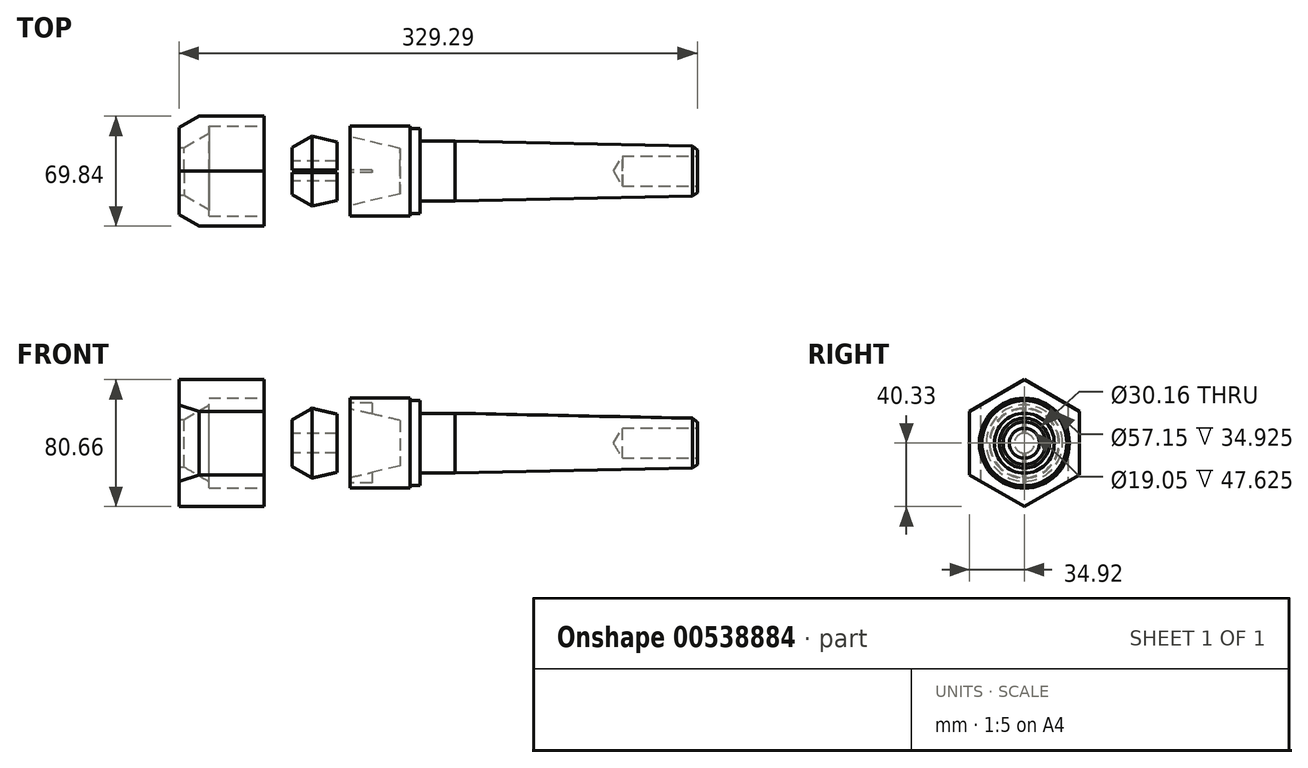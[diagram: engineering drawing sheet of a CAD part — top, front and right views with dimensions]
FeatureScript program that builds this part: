
annotation { "Feature Type Name" : "Feature", "Feature Type Description" : "" }
export const myFeature = defineFeature(function(context is Context, id is Id, definition is map)
    precondition{}
    {
        {
            var Q0;
            Q0=qCreatedBy(makeId("Front.planeOp"),FACE);
            var sketch = newSketch(context, id + "F0", { "sketchPlane" : qUnion([Q0])});
            skLineSegment(sketch, "E0.bottom", {"start": v(31.75, 0) * mm, "end": v(38.1, 0) * mm});
            skLineSegment(sketch, "E0.top", {"start": v(0, 28.58) * mm, "end": v(38.1, 28.58) * mm});
            skLineSegment(sketch, "E0.left", {"start": v(0, 21.83) * mm, "end": v(0, 28.58) * mm});
            skLineSegment(sketch, "E0.right", {"start": v(38.1, 0) * mm, "end": v(38.1, 28.58) * mm});
            skLineSegment(sketch, "E1.bottom", {"start": v(38.1, 0) * mm, "end": v(44.45, 0) * mm});
            skLineSegment(sketch, "E1.top", {"start": v(38.1, 26.99) * mm, "end": v(44.45, 26.99) * mm});
            skLineSegment(sketch, "E1.left", {"start": v(38.1, 0) * mm, "end": v(38.1, 26.99) * mm});
            skLineSegment(sketch, "E1.right", {"start": v(44.45, 0) * mm, "end": v(44.45, 26.99) * mm});
            skLineSegment(sketch, "E2.bottom", {"start": v(44.45, 0) * mm, "end": v(217.49, 0) * mm});
            skLineSegment(sketch, "E2.top", {"start": v(44.45, 19.02) * mm, "end": v(66.67, 19.02) * mm});
            skLineSegment(sketch, "E2.left", {"start": v(44.45, 0) * mm, "end": v(44.45, 19.02) * mm});
            skLineSegment(sketch, "E3.bottom", {"start": v(217.49, 0) * mm, "end": v(220.66, 0) * mm});
            skLineSegment(sketch, "E3.right", {"start": v(220.66, 0) * mm, "end": v(220.66, 13.5) * mm});
            skPoint(sketch, "E4", {"position": v(217.49, 15.88) * mm});
            skLineSegment(sketch, "E5", {"start": v(66.67, 19.02) * mm, "end": v(217.49, 15.87) * mm});
            skLineSegment(sketch, "E6", {"start": v(220.66, 13.5) * mm, "end": v(217.49, 15.88) * mm});
            skPoint(sketch, "E7.end.orphan", {"position": v(66.17, 0) * mm});
            skLineSegment(sketch, "E8", {"start": v(31.75, 0) * mm, "end": v(31.75, 14.5) * mm});
            skLineSegment(sketch, "E9", {"start": v(0, 21.83) * mm, "end": v(31.75, 14.5) * mm});
            skPoint(sketch, "E10", {"position": v(31.75, 14.5) * mm});
            skPoint(sketch, "E11.orphan", {"position": v(66.17, 6.55) * mm});
            skSolve(sketch);
        }
        {
            var Q0;
            Q0=makeQuery(id+"F0.imprint","IMPRINT",FACE,{"disambiguationData":[TD([[makeQuery(id+"F0.imprint","IMPRINT",EDGE,{"derivedFrom":sQuery(id+"F0.wireOp",EDGE,"E1.bottom")}),1.0]])]});
            var Q1;
            Q1=makeQuery(id+"F0.imprint","IMPRINT",FACE,{"disambiguationData":[TD([[makeQuery(id+"F0.imprint","IMPRINT",EDGE,{"derivedFrom":sQuery(id+"F0.wireOp",EDGE,"E0.bottom")}),1.0]])]});
            var Q2;
            Q2=makeQuery(id+"F0.imprint","IMPRINT",FACE,{"disambiguationData":[TD([[makeQuery(id+"F0.imprint","IMPRINT",EDGE,{"derivedFrom":sQuery(id+"F0.wireOp",EDGE,"E2.bottom")}),1.0]])]});
            var Q3;
            Q3=sQuery(id+"F0.wireOp",EDGE,"E2.bottom");
            revolve(context, id + "F1", {"entities" : qUnion([Q0, Q1, Q2]), "axis" : qUnion([Q3]), "revolveType" : RevolveType.FULL});
        }
        {
            var Q0;
            Q0=makeQuery(id+"F1.opRevolve","SWEPT_FACE",FACE,{"disambiguationData":[OSD([sQuery(id+"F0.wireOp",EDGE,"E3.right")])]});
            var sketch = newSketch(context, id + "F2", { "sketchPlane" : qUnion([Q0])});
            skCircle(sketch, "E12", {"center": v(0, 0) * mm, "radius": 9.53 * mm});
            skSolve(sketch);
        }
        {
            var Q0;
            Q0=sQuery(id+"F2.wireOp",VERTEX,"E12.center");
            var Q1;
            Q1=makeQuery(id+"F1.opRevolve","SWEPT_BODY",BODY,{"disambiguationData":[OSD([sQuery(id+"F0.wireOp",EDGE,"E0.bottom"),sQuery(id+"F0.wireOp",EDGE,"E0.top"),sQuery(id+"F0.wireOp",EDGE,"E0.left"),sQuery(id+"F0.wireOp",EDGE,"E0.right"),sQuery(id+"F0.wireOp",EDGE,"E1.bottom"),sQuery(id+"F0.wireOp",EDGE,"E1.top"),sQuery(id+"F0.wireOp",EDGE,"E1.right"),sQuery(id+"F0.wireOp",EDGE,"E2.bottom"),sQuery(id+"F0.wireOp",EDGE,"E2.top"),sQuery(id+"F0.wireOp",EDGE,"E3.bottom"),sQuery(id+"F0.wireOp",EDGE,"E3.right"),sQuery(id+"F0.wireOp",EDGE,"E5"),sQuery(id+"F0.wireOp",EDGE,"E6"),sQuery(id+"F0.wireOp",EDGE,"E8"),sQuery(id+"F0.wireOp",EDGE,"E9")])]});
            hole(context, id + "F3", {"style" : HoleStyle.SIMPLE, "endStyle" : HoleEndStyle.BLIND, "holeDiameter" : 19.05 * mm, "holeDepth" : 47.62 * mm, "isTappedThrough" : true, "tappedDepth" : 12.7 * mm, "tapClearance" : 3, "locations" : qUnion([Q0]), "scope" : qUnion([Q1])});
        }
        {
            var Q0;
            Q0=qCreatedBy(makeId("Front.planeOp"),FACE);
            var sketch = newSketch(context, id + "F4", { "sketchPlane" : qUnion([Q0])});
            skLineSegment(sketch, "E13.bottom", {"start": v(-8.23, 0) * mm, "end": v(-24.1, 0) * mm});
            skLineSegment(sketch, "E13.left", {"start": v(-8.23, 0) * mm, "end": v(-8.23, 7.13) * mm});
            skLineSegment(sketch, "E14.bottom", {"start": v(-24.1, 0) * mm, "end": v(-36.8, 0) * mm});
            skLineSegment(sketch, "E14.right", {"start": v(-36.8, 0) * mm, "end": v(-36.8, 14.9) * mm});
            skLineSegment(sketch, "E15", {"start": v(-24.1, 22.23) * mm, "end": v(-36.8, 14.9) * mm});
            skPoint(sketch, "E15.endSnap0", {"position": v(-24.1, 11.11) * mm});
            skLineSegment(sketch, "E16", {"start": v(-24.1, 22.23) * mm, "end": v(-8.23, 18.56) * mm});
            skLineSegment(sketch, "E17", {"start": v(-8.23, 7.13) * mm, "end": v(-8.23, 18.56) * mm});
            skPoint(sketch, "E18.orphan", {"position": v(-43.35, 11.11) * mm});
            skSolve(sketch);
        }
        {
            var Q0;
            Q0 = qSketchRegion(id + "F4", true);
            var Q1;
            Q1=sQuery(id+"F4.wireOp",EDGE,"E14.bottom");
            revolve(context, id + "F5", {"entities" : qUnion([Q0]), "axis" : qUnion([Q1]), "revolveType" : RevolveType.FULL});
        }
        {
            var Q0;
            Q0=makeQuery(id+"F5.opRevolve","SWEPT_FACE",FACE,{"disambiguationData":[OSD([sQuery(id+"F4.wireOp",EDGE,"E14.right")])]});
            var sketch = newSketch(context, id + "F6", { "sketchPlane" : qUnion([Q0])});
            skCircle(sketch, "E19", {"center": v(0, 0) * mm, "radius": 6.35 * mm});
            skSolve(sketch);
        }
        {
            var Q0;
            Q0 = qSketchRegion(id + "F6", true);
            extrude(context, id + "F7", {"entities" : qUnion([Q0]), "operationType" : NewBodyOperationType.REMOVE, "oppositeDirection" : true, "depth" : 44.45 * mm, "offsetDistance" : 25.4 * mm});
        }
        {
            var Q0;
            Q0=makeQuery(id+"F5.opRevolve","SWEPT_FACE",FACE,{"disambiguationData":[OSD([sQuery(id+"F4.wireOp",EDGE,"E14.right")])]});
            var sketch = newSketch(context, id + "F8", { "sketchPlane" : qUnion([Q0])});
            skLineSegment(sketch, "E20.bottom", {"start": v(-0.8, 25.4) * mm, "end": v(0.8, 25.4) * mm});
            skLineSegment(sketch, "E20.top", {"start": v(-0.8, -25.4) * mm, "end": v(0.8, -25.4) * mm});
            skLineSegment(sketch, "E20.left", {"start": v(-0.8, 25.4) * mm, "end": v(-0.8, -25.4) * mm});
            skLineSegment(sketch, "E20.right", {"start": v(0.8, 25.4) * mm, "end": v(0.8, -25.4) * mm});
            skPoint(sketch, "E20.middle", {"position": v(0, 0) * mm});
            skSolve(sketch);
        }
        {
            var Q0;
            Q0 = qSketchRegion(id + "F8", true);
            extrude(context, id + "F9", {"entities" : qUnion([Q0]), "operationType" : NewBodyOperationType.REMOVE, "oppositeDirection" : true, "depth" : 50.8 * mm, "offsetDistance" : 25.4 * mm});
        }
        {
            var Q0;
            Q0=qCreatedBy(makeId("Front.planeOp"),FACE);
            var sketch = newSketch(context, id + "F10", { "sketchPlane" : qUnion([Q0])});
            skLineSegment(sketch, "E21.bottom", {"start": v(-54.66, 44.45) * mm, "end": v(-108.63, 44.45) * mm});
            skLineSegment(sketch, "E21.top", {"start": v(-54.66, -44.45) * mm, "end": v(-108.63, -44.45) * mm});
            skLineSegment(sketch, "E21.left", {"start": v(-54.66, 44.45) * mm, "end": v(-54.66, -44.45) * mm});
            skLineSegment(sketch, "E21.right", {"start": v(-108.63, 44.45) * mm, "end": v(-108.63, -44.45) * mm});
            skPoint(sketch, "E21.middle", {"position": v(-81.64, 0) * mm});
            skSolve(sketch);
        }
        {
            var Q0;
            Q0 = qSketchRegion(id + "F10", true);
            extrude(context, id + "F11", {"entities" : qUnion([Q0]), "endBound" : BoundingType.SYMMETRIC, "depth" : 69.85 * mm, "offsetDistance" : 25.4 * mm});
        }
        {
            var Q0;
            Q0=makeQuery(id+"F11.opExtrude","SWEPT_FACE",FACE,{"disambiguationData":[OSD([sQuery(id+"F10.wireOp",EDGE,"E21.right")])]});
            var sketch = newSketch(context, id + "F12", { "sketchPlane" : qUnion([Q0])});
            skCircle(sketch, "E22.cCircle", {"center": v(0, 0) * mm, "radius": 40.33 * mm, "construction": true});
            skLineSegment(sketch, "E22.0", {"start": v(34.93, -20.16) * mm, "end": v(0, -40.33) * mm});
            skLineSegment(sketch, "E22.1", {"start": v(0, -40.33) * mm, "end": v(-34.93, -20.16) * mm});
            skLineSegment(sketch, "E22.2", {"start": v(-34.93, -20.16) * mm, "end": v(-34.93, 20.16) * mm});
            skLineSegment(sketch, "E22.3", {"start": v(-34.93, 20.16) * mm, "end": v(0, 40.33) * mm});
            skLineSegment(sketch, "E22.4", {"start": v(0, 40.33) * mm, "end": v(34.93, 20.16) * mm});
            skLineSegment(sketch, "E22.5", {"start": v(34.93, 20.16) * mm, "end": v(34.93, -20.16) * mm});
            skSolve(sketch);
        }
        {
            var Q0;
            {var subQ4=sQuery(id+"F12.wireOp",EDGE,"E22.3");Q0=makeQuery(id+"F12.imprint","IMPRINT",FACE,{"disambiguationData":[TD([[makeQuery(id+"F12.imprint","IMPRINT",EDGE,{"derivedFrom":subQ4}),1.0]])]});}
            var Q1;
            {var subQ4=sQuery(id+"F12.wireOp",EDGE,"E22.0");Q1=makeQuery(id+"F12.imprint","IMPRINT",FACE,{"disambiguationData":[TD([[makeQuery(id+"F12.imprint","IMPRINT",EDGE,{"derivedFrom":subQ4}),1.0]])]});}
            extrude(context, id + "F13", {"entities" : qUnion([Q0, Q1]), "operationType" : NewBodyOperationType.REMOVE, "oppositeDirection" : true, "depth" : 53.97 * mm, "offsetDistance" : 25.4 * mm});
        }
        {
            var Q0;
            Q0=makeQuery(id+"F13.boolean.opBoolean","COPY",EDGE,{"derivedFrom":makeQuery(id+"F13.opExtrude","CAP_EDGE",EDGE,{"disambiguationData":[OSD([sQuery(id+"F12.wireOp",EDGE,"E22.4")])],"isStart":true})});
            var Q1;
            Q1=makeQuery(id+"F11.opExtrude","CAP_EDGE",EDGE,{"disambiguationData":[OSD([sQuery(id+"F10.wireOp",EDGE,"E21.right")])],"isStart":false});
            var Q2;
            Q2=makeQuery(id+"F13.boolean.opBoolean","COPY",EDGE,{"derivedFrom":makeQuery(id+"F13.opExtrude","CAP_EDGE",EDGE,{"disambiguationData":[OSD([sQuery(id+"F12.wireOp",EDGE,"E22.0")])],"isStart":true})});
            var Q3;
            Q3=makeQuery(id+"F13.boolean.opBoolean","COPY",EDGE,{"derivedFrom":makeQuery(id+"F13.opExtrude","CAP_EDGE",EDGE,{"disambiguationData":[OSD([sQuery(id+"F12.wireOp",EDGE,"E22.1")])],"isStart":true})});
            var Q4;
            Q4=makeQuery(id+"F11.opExtrude","CAP_EDGE",EDGE,{"disambiguationData":[OSD([sQuery(id+"F10.wireOp",EDGE,"E21.right")])],"isStart":true});
            var Q5;
            Q5=makeQuery(id+"F13.boolean.opBoolean","COPY",EDGE,{"derivedFrom":makeQuery(id+"F13.opExtrude","CAP_EDGE",EDGE,{"disambiguationData":[OSD([sQuery(id+"F12.wireOp",EDGE,"E22.3")])],"isStart":true})});
            chamfer(context, id + "F14", {"entities" : qUnion([Q0, Q1, Q2, Q3, Q4, Q5]), "chamferType" : ChamferType.OFFSET_ANGLE, "width" : 12.7 * mm, "oppositeDirection" : false, "angle" : 30 * degree, "tangentPropagation" : true});
        }
        {
            var Q0;
            Q0=makeQuery(id+"F11.opExtrude","SWEPT_FACE",FACE,{"disambiguationData":[OSD([sQuery(id+"F10.wireOp",EDGE,"E21.left")])]});
            var sketch = newSketch(context, id + "F15", { "sketchPlane" : qUnion([Q0])});
            skCircle(sketch, "E23", {"center": v(0, 0) * mm, "radius": 15.08 * mm});
            skSolve(sketch);
        }
        {
            var Q0;
            Q0=makeQuery(id+"F15.imprint","IMPRINT",FACE,{"disambiguationData":[TD([[makeQuery(id+"F15.imprint","IMPRINT",EDGE,{"derivedFrom":sQuery(id+"F15.wireOp",EDGE,"E23")}),1.0]])]});
            extrude(context, id + "F16", {"entities" : qUnion([Q0]), "operationType" : NewBodyOperationType.REMOVE, "endBound" : BoundingType.THROUGH_ALL, "oppositeDirection" : true, "depth" : 25.4 * mm, "offsetDistance" : 25.4 * mm});
        }
        {
            var Q0;
            Q0=makeQuery(id+"F15.imprint","IMPRINT",FACE,{"disambiguationData":[TD([[makeQuery(id+"F15.imprint","IMPRINT",EDGE,{"derivedFrom":sQuery(id+"F15.wireOp",EDGE,"E23")}),-1.0]])]});
            var sketch = newSketch(context, id + "F17", { "sketchPlane" : qUnion([Q0])});
            skCircle(sketch, "E24", {"center": v(0, 0) * mm, "radius": 28.58 * mm});
            skSolve(sketch);
        }
        {
            var Q0;
            Q0 = qSketchRegion(id + "F17", true);
            extrude(context, id + "F18", {"entities" : qUnion([Q0]), "operationType" : NewBodyOperationType.REMOVE, "oppositeDirection" : true, "depth" : 34.92 * mm, "offsetDistance" : 25.4 * mm});
        }
        {
            var Q0;
            Q0=qCreatedBy(makeId("Front.planeOp"),FACE);
            var sketch = newSketch(context, id + "F19", { "sketchPlane" : qUnion([Q0])});
            skLineSegment(sketch, "E25", {"start": v(-105.46, 19.01) * mm, "end": v(-105.46, 0) * mm});
            skPoint(sketch, "E26.start.orphan", {"position": v(-51.08, 0) * mm});
            skLineSegment(sketch, "E27", {"start": v(-87.1, 0) * mm, "end": v(-92.76, 0) * mm});
            skLineSegment(sketch, "E28", {"start": v(-87.1, 15.08) * mm, "end": v(-105.46, 15.08) * mm});
            skLineSegment(sketch, "E29", {"start": v(-92.76, 22.41) * mm, "end": v(-92.76, 15.08) * mm});
            skLineSegment(sketch, "E30", {"start": v(-105.46, 15.08) * mm, "end": v(-87.1, 25.68) * mm});
            skLineSegment(sketch, "E31", {"start": v(-105.46, -15.08) * mm, "end": v(-67.53, -36.98) * mm});
            skLineSegment(sketch, "E32", {"start": v(-67.53, -36.98) * mm, "end": v(-105.46, -15.08) * mm});
            skLineSegment(sketch, "E33", {"start": v(-97.2, 19.85) * mm, "end": v(-105.46, 15.08) * mm});
            skLineSegment(sketch, "E34", {"start": v(-87.1, 22.43) * mm, "end": v(-87.1, 25.68) * mm});
            skLineSegment(sketch, "E35", {"start": v(-87.1, 25.68) * mm, "end": v(-87.1, 0) * mm});
            skLineSegment(sketch, "E36.trimOffspring", {"start": v(-131.58, 0) * mm, "end": v(-133.2, 0) * mm});
            skLineSegment(sketch, "E37.trimOffspring", {"start": v(-131.58, 0) * mm, "end": v(-133.2, 0.94) * mm});
            skLineSegment(sketch, "E38", {"start": v(-87.1, 0) * mm, "end": v(-105.46, 0) * mm});
            skLineSegment(sketch, "E39", {"start": v(-105.46, 0) * mm, "end": v(-105.46, 15.08) * mm});
            skSolve(sketch);
        }
        {
            var Q0;
            Q0 = qSketchRegion(id + "F19", true);
            var Q1;
            Q1=sQuery(id+"F19.wireOp",EDGE,"E38");
            revolve(context, id + "F20", {"operationType" : NewBodyOperationType.REMOVE, "entities" : qUnion([Q0]), "axis" : qUnion([Q1]), "revolveType" : RevolveType.FULL, "oppositeDirection" : true});
        }
    });
